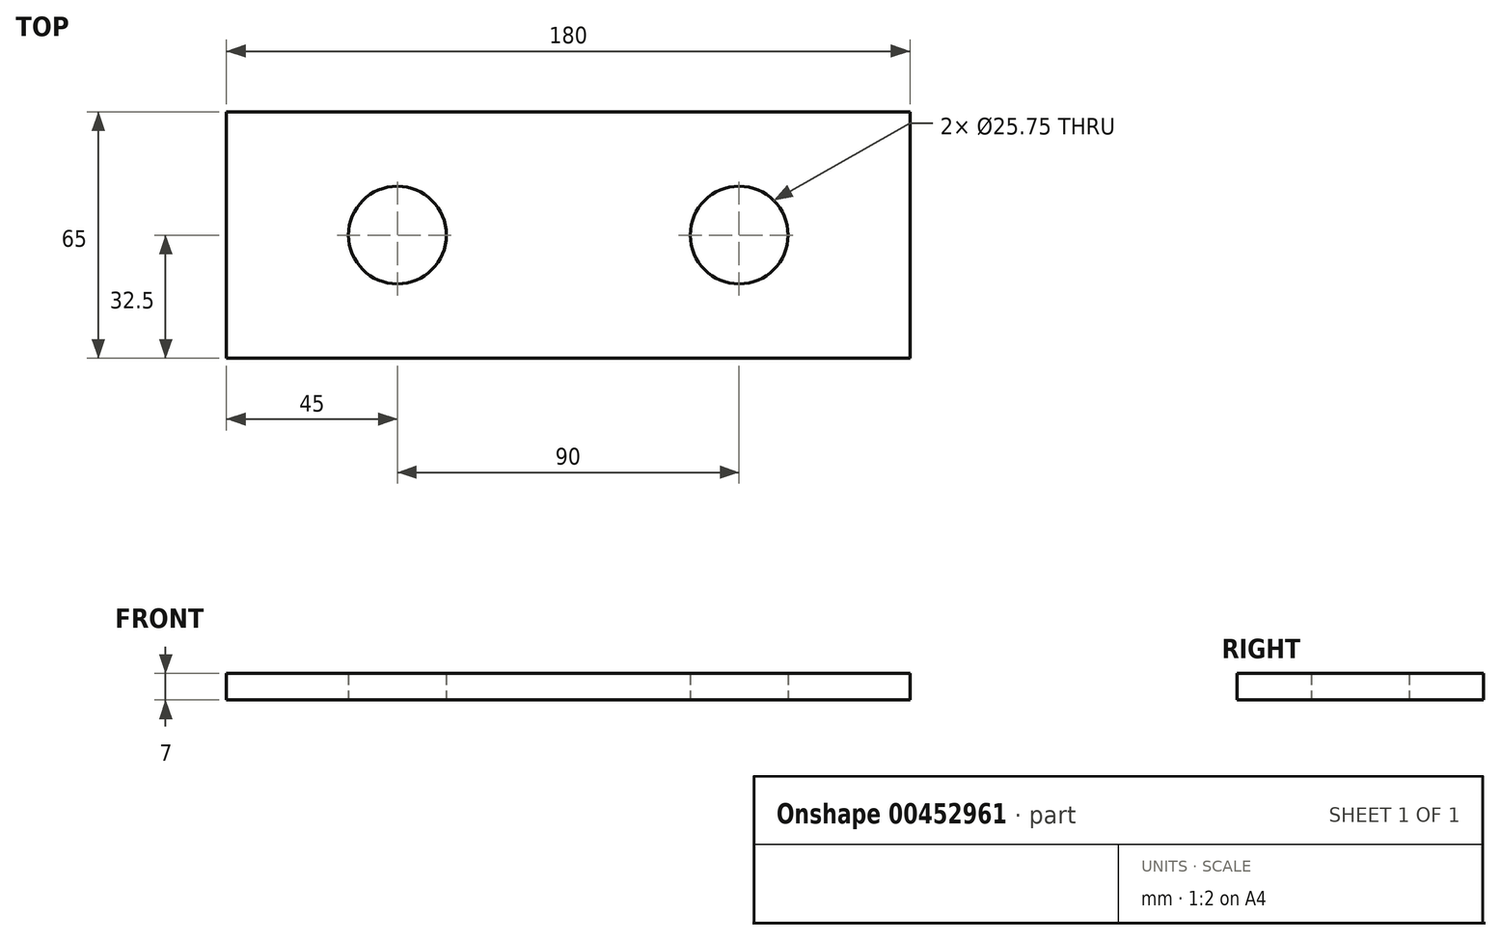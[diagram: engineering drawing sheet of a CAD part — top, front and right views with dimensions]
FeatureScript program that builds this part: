
annotation { "Feature Type Name" : "Feature", "Feature Type Description" : "" }
export const myFeature = defineFeature(function(context is Context, id is Id, definition is map)
    precondition{}
    {
        {
            var Q0;
            Q0=qCreatedBy(makeId("Top.planeOp"),FACE);
            var sketch = newSketch(context, id + "F0", { "sketchPlane" : qUnion([Q0])});
            skLineSegment(sketch, "E0.bottom", {"start": v(-90, 32.5) * mm, "end": v(90, 32.5) * mm});
            skLineSegment(sketch, "E0.top", {"start": v(-90, -32.5) * mm, "end": v(90, -32.5) * mm});
            skLineSegment(sketch, "E0.left", {"start": v(-90, 32.5) * mm, "end": v(-90, -32.5) * mm});
            skLineSegment(sketch, "E0.right", {"start": v(90, 32.5) * mm, "end": v(90, -32.5) * mm});
            skCircle(sketch, "E1", {"center": v(45, 0) * mm, "radius": 12.88 * mm});
            skCircle(sketch, "E2", {"center": v(-45, 0) * mm, "radius": 12.88 * mm});
            skSolve(sketch);
        }
        {
            var Q0;
            Q0 = qSketchRegion(id + "F0", true);
            extrude(context, id + "F1", {"entities" : qUnion([Q0]), "depth" : 7 * mm});
        }
    });
